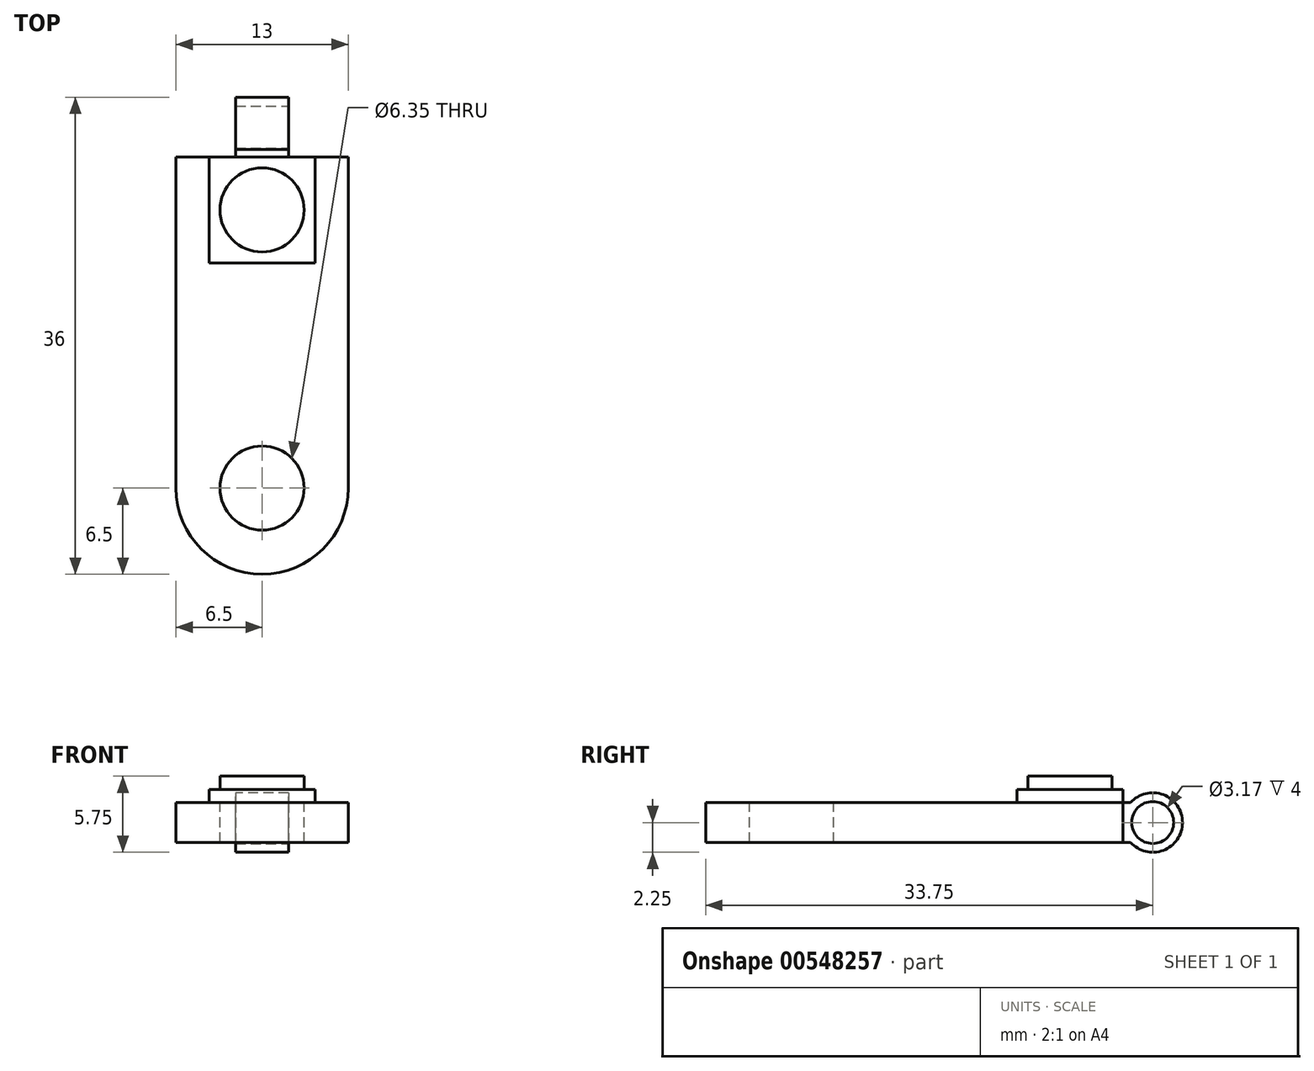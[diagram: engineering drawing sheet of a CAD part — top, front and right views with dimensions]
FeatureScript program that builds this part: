
annotation { "Feature Type Name" : "Feature", "Feature Type Description" : "" }
export const myFeature = defineFeature(function(context is Context, id is Id, definition is map)
    precondition{}
    {
        {
            var Q0;
            Q0=qCreatedBy(makeId("Top.planeOp"),FACE);
            var sketch = newSketch(context, id + "F0", { "sketchPlane" : qUnion([Q0])});
            skArc(sketch, "E0", {"start": v(-6.5, 0) * mm, "mid": v(0, -6.5) * mm, "end": v(6.5, 0) * mm});
            skLineSegment(sketch, "E1", {"start": v(-6.5, 0) * mm, "end": v(-6.5, 25) * mm});
            skLineSegment(sketch, "E2", {"start": v(-6.5, 25) * mm, "end": v(6.5, 25) * mm});
            skLineSegment(sketch, "E3", {"start": v(6.5, 25) * mm, "end": v(6.5, 0) * mm});
            skSolve(sketch);
        }
        {
            var Q0;
            Q0 = qSketchRegion(id + "F0", true);
            extrude(context, id + "F1", {"entities" : qUnion([Q0]), "endBound" : BoundingType.SYMMETRIC, "depth" : 3 * mm, "offsetDistance" : 25 * mm});
        }
        {
            var Q0;
            Q0=makeQuery(id+"F1.opExtrude","CAP_FACE",FACE,{"disambiguationData":[OSD([sQuery(id+"F0.wireOp",EDGE,"E0"),sQuery(id+"F0.wireOp",EDGE,"E1"),sQuery(id+"F0.wireOp",EDGE,"E2"),sQuery(id+"F0.wireOp",EDGE,"E3")])],"isStart":false});
            var sketch = newSketch(context, id + "F2", { "sketchPlane" : qUnion([Q0])});
            skLineSegment(sketch, "E4.bottom", {"start": v(-4, 25) * mm, "end": v(4, 25) * mm});
            skLineSegment(sketch, "E4.top", {"start": v(-4, 17) * mm, "end": v(4, 17) * mm});
            skLineSegment(sketch, "E4.left", {"start": v(-4, 25) * mm, "end": v(-4, 17) * mm});
            skLineSegment(sketch, "E4.right", {"start": v(4, 25) * mm, "end": v(4, 17) * mm});
            skSolve(sketch);
        }
        {
            var Q0;
            Q0 = qSketchRegion(id + "F2", true);
            extrude(context, id + "F3", {"entities" : qUnion([Q0]), "operationType" : NewBodyOperationType.ADD, "depth" : 1 * mm, "offsetDistance" : 25 * mm});
        }
        {
            var Q0;
            Q0=makeQuery(id+"F3.opExtrude","CAP_FACE",FACE,{"disambiguationData":[OSD([sQuery(id+"F2.wireOp",EDGE,"E4.bottom"),sQuery(id+"F2.wireOp",EDGE,"E4.top"),sQuery(id+"F2.wireOp",EDGE,"E4.left"),sQuery(id+"F2.wireOp",EDGE,"E4.right")])],"isStart":false});
            var sketch = newSketch(context, id + "F4", { "sketchPlane" : qUnion([Q0])});
            skLineSegment(sketch, "E5", {"start": v(0, 17) * mm, "end": v(0, 25) * mm, "construction": true});
            skCircle(sketch, "E6", {"center": v(0, 21) * mm, "radius": 3.17 * mm});
            skSolve(sketch);
        }
        {
            var Q0;
            Q0 = qSketchRegion(id + "F4", true);
            extrude(context, id + "F5", {"entities" : qUnion([Q0]), "operationType" : NewBodyOperationType.ADD, "depth" : 1 * mm, "offsetDistance" : 25 * mm});
        }
        {
            var Q0;
            Q0=qCreatedBy(makeId("Right.planeOp"),FACE);
            var sketch = newSketch(context, id + "F6", { "sketchPlane" : qUnion([Q0])});
            skLineSegment(sketch, "E7.0", {"start": v(25, 1.5) * mm, "end": v(25, -1.5) * mm});
            skArc(sketch, "E8", {"start": v(25.57, -1.5) * mm, "mid": v(29.5, 0) * mm, "end": v(25.57, 1.5) * mm});
            skLineSegment(sketch, "E9", {"start": v(25, 1.5) * mm, "end": v(25.57, 1.5) * mm});
            skLineSegment(sketch, "E10", {"start": v(25, -1.5) * mm, "end": v(25.57, -1.5) * mm});
            skSolve(sketch);
        }
        {
            var Q0;
            Q0=makeQuery(id+"F6.imprint","IMPRINT",FACE,{"disambiguationData":[TD([[makeQuery(id+"F6.imprint","IMPRINT",EDGE,{"derivedFrom":sQuery(id+"F6.wireOp",EDGE,"E7.0")}),1.0]])]});
            extrude(context, id + "F7", {"entities" : qUnion([Q0]), "operationType" : NewBodyOperationType.ADD, "endBound" : BoundingType.SYMMETRIC, "depth" : 4 * mm, "offsetDistance" : 25 * mm});
        }
        {
            var Q0;
            Q0=makeQuery(id+"F7.opExtrude","CAP_FACE",FACE,{"disambiguationData":[OSD([sQuery(id+"F6.wireOp",EDGE,"E7.0"),sQuery(id+"F6.wireOp",EDGE,"E8"),sQuery(id+"F6.wireOp",EDGE,"E9"),sQuery(id+"F6.wireOp",EDGE,"E10")])],"isStart":false});
            var sketch = newSketch(context, id + "F8", { "sketchPlane" : qUnion([Q0])});
            skPoint(sketch, "E11", {"position": v(27.25, 0) * mm});
            skSolve(sketch);
        }
        {
            var Q0;
            Q0=sQuery(id+"F8.wireOp",VERTEX,"E11");
            var Q1;
            Q1=makeQuery(id+"F1.opExtrude","SWEPT_BODY",BODY,{"disambiguationData":[OSD([sQuery(id+"F0.wireOp",EDGE,"E0"),sQuery(id+"F0.wireOp",EDGE,"E1"),sQuery(id+"F0.wireOp",EDGE,"E2"),sQuery(id+"F0.wireOp",EDGE,"E3")])]});
            hole(context, id + "F9", {"style" : HoleStyle.SIMPLE, "endStyle" : HoleEndStyle.THROUGH, "holeDiameter" : 3.17 * mm, "isTappedThrough" : true, "tappedDepth" : 12 * mm, "tapClearance" : 3, "locations" : qUnion([Q0]), "scope" : qUnion([Q1])});
        }
        {
            var Q0;
            Q0=makeQuery(id+"F1.opExtrude","CAP_FACE",FACE,{"disambiguationData":[OSD([sQuery(id+"F0.wireOp",EDGE,"E0"),sQuery(id+"F0.wireOp",EDGE,"E1"),sQuery(id+"F0.wireOp",EDGE,"E2"),sQuery(id+"F0.wireOp",EDGE,"E3")])],"isStart":false});
            var sketch = newSketch(context, id + "F10", { "sketchPlane" : qUnion([Q0])});
            skPoint(sketch, "E12", {"position": v(0, 0) * mm});
            skSolve(sketch);
        }
        {
            var Q0;
            Q0=sQuery(id+"F10.wireOp",VERTEX,"E12");
            var Q1;
            Q1=makeQuery(id+"F1.opExtrude","SWEPT_BODY",BODY,{"disambiguationData":[OSD([sQuery(id+"F0.wireOp",EDGE,"E0"),sQuery(id+"F0.wireOp",EDGE,"E1"),sQuery(id+"F0.wireOp",EDGE,"E2"),sQuery(id+"F0.wireOp",EDGE,"E3")])]});
            hole(context, id + "F11", {"style" : HoleStyle.SIMPLE, "endStyle" : HoleEndStyle.THROUGH, "holeDiameter" : 6.35 * mm, "isTappedThrough" : true, "tappedDepth" : 12 * mm, "tapClearance" : 3, "locations" : qUnion([Q0]), "scope" : qUnion([Q1])});
        }
    });
